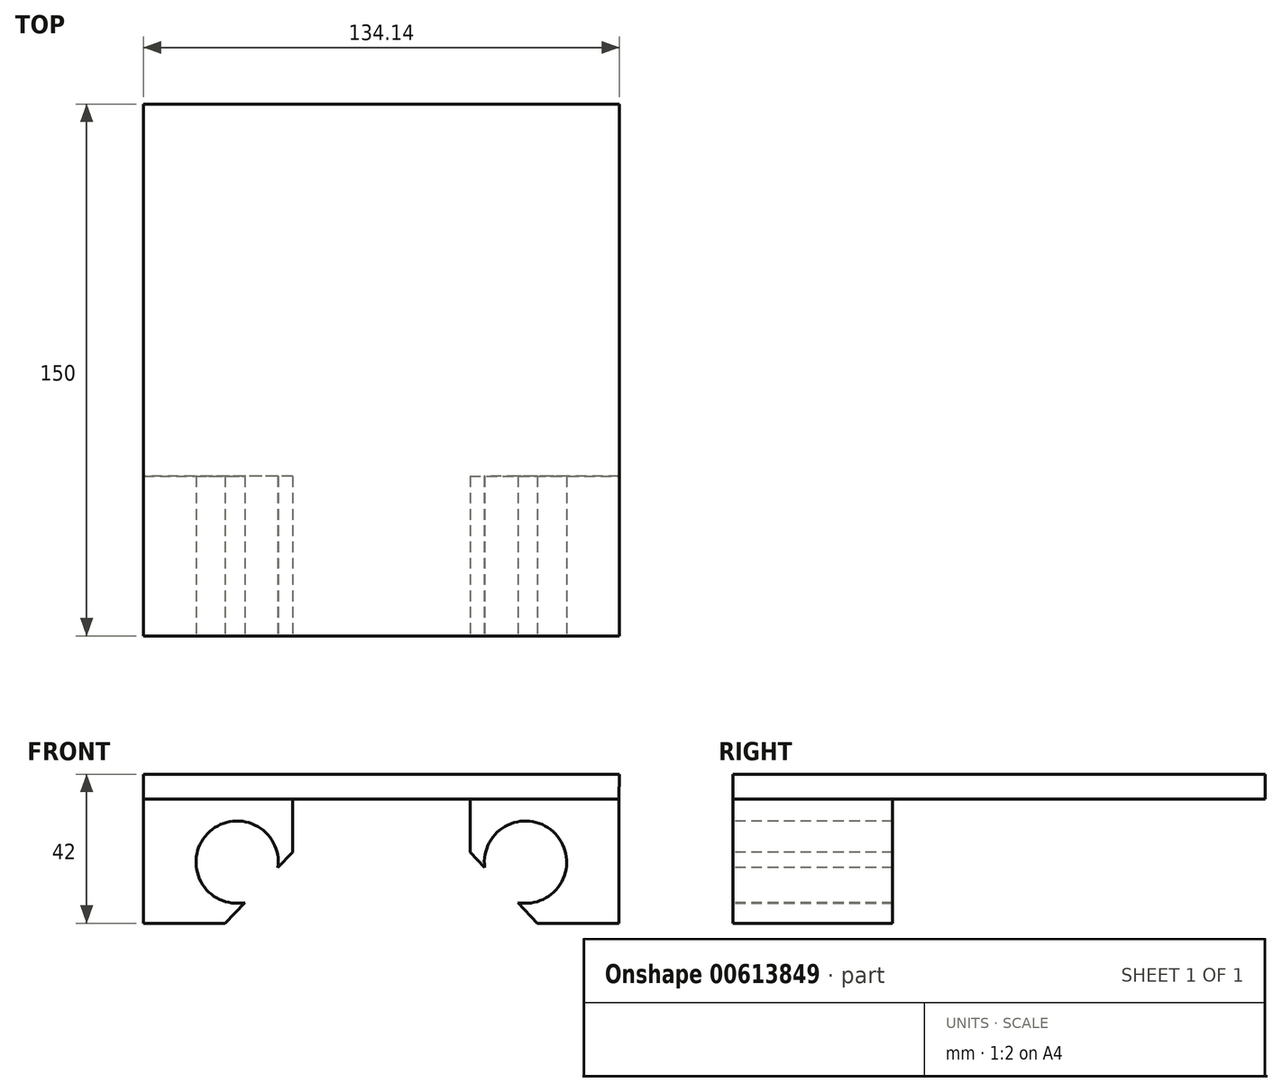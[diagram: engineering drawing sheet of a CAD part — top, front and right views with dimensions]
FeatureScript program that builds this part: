
annotation { "Feature Type Name" : "Feature", "Feature Type Description" : "" }
export const myFeature = defineFeature(function(context is Context, id is Id, definition is map)
    precondition{}
    {
        {
            var Q0;
            Q0=qCreatedBy(makeId("Front.planeOp"),FACE);
            var sketch = newSketch(context, id + "F0", { "sketchPlane" : qUnion([Q0])});
            skLineSegment(sketch, "E0", {"start": v(0, 35) * mm, "end": v(67, 35) * mm});
            skLineSegment(sketch, "E1", {"start": v(67, 35) * mm, "end": v(67, 0) * mm});
            skLineSegment(sketch, "E2", {"start": v(67, 0) * mm, "end": v(44, 0) * mm});
            skLineSegment(sketch, "E3", {"start": v(44, 0) * mm, "end": v(38.5, 5.8) * mm});
            skPoint(sketch, "E4", {"position": v(25, 35) * mm});
            skLineSegment(sketch, "E5", {"start": v(25, 35) * mm, "end": v(25, 20) * mm});
            skLineSegment(sketch, "E6", {"start": v(25, 20) * mm, "end": v(29.13, 15.65) * mm});
            skLineSegment(sketch, "E7", {"start": v(29.13, 15.65) * mm, "end": v(38.5, 5.8) * mm, "construction": true});
            skArc(sketch, "E8", {"start": v(38.5, 5.8) * mm, "mid": v(49.05, 25.2) * mm, "end": v(29.13, 15.65) * mm});
            skLineSegment(sketch, "E9", {"start": v(0, 35) * mm, "end": v(0, 42) * mm});
            skLineSegment(sketch, "E10", {"start": v(0, 42) * mm, "end": v(67.07, 42) * mm});
            skLineSegment(sketch, "E11", {"start": v(67.07, 42) * mm, "end": v(67, 35) * mm});
            skLineSegment(sketch, "E12.MirrorCS", {"start": v(0, 42) * mm, "end": v(-67.07, 42) * mm});
            skLineSegment(sketch, "E13.MirrorCS", {"start": v(0, 35) * mm, "end": v(-67, 35) * mm});
            skLineSegment(sketch, "E14.MirrorCS", {"start": v(-67.07, 42) * mm, "end": v(-67, 35) * mm});
            skLineSegment(sketch, "E15.MirrorCS", {"start": v(-67, 35) * mm, "end": v(-67, 0) * mm});
            skLineSegment(sketch, "E16.MirrorCS", {"start": v(-25, 35) * mm, "end": v(-25, 20) * mm});
            skLineSegment(sketch, "E17.MirrorCS", {"start": v(-25, 20) * mm, "end": v(-29.13, 15.65) * mm});
            skArc(sketch, "E18.MirrorCS", {"start": v(-38.5, 5.8) * mm, "mid": v(-49.05, 25.2) * mm, "end": v(-29.13, 15.65) * mm});
            skLineSegment(sketch, "E19.MirrorCS", {"start": v(-44, 0) * mm, "end": v(-38.5, 5.8) * mm});
            skLineSegment(sketch, "E20.MirrorCS", {"start": v(-67, 0) * mm, "end": v(-44, 0) * mm});
            skSolve(sketch);
        }
        {
            var Q0;
            {var subQ1=sQuery(id+"F0.wireOp",EDGE,"E15.MirrorCS");Q0=makeQuery(id+"F0.imprint","IMPRINT",FACE,{"disambiguationData":[TD([[makeQuery(id+"F0.imprint","IMPRINT",EDGE,{"derivedFrom":subQ1}),1.0]])]});}
            var Q1;
            {var subQ0=sQuery(id+"F0.wireOp",EDGE,"E1");Q1=makeQuery(id+"F0.imprint","IMPRINT",FACE,{"disambiguationData":[TD([[makeQuery(id+"F0.imprint","IMPRINT",EDGE,{"derivedFrom":subQ0}),-1.0]])]});}
            extrude(context, id + "F1", {"entities" : qUnion([Q0, Q1]), "oppositeDirection" : true, "depth" : 45 * mm, "offsetDistance" : 25 * mm});
        }
        {
            var Q0;
            {var subQ0=sQuery(id+"F0.wireOp",EDGE,"E9");Q0=makeQuery(id+"F0.imprint","IMPRINT",FACE,{"disambiguationData":[TD([[makeQuery(id+"F0.imprint","IMPRINT",EDGE,{"derivedFrom":subQ0}),-1.0]])]});}
            var Q1;
            {var subQ1=sQuery(id+"F0.wireOp",EDGE,"E9");Q1=makeQuery(id+"F0.imprint","IMPRINT",FACE,{"disambiguationData":[TD([[makeQuery(id+"F0.imprint","IMPRINT",EDGE,{"derivedFrom":subQ1}),1.0]])]});}
            extrude(context, id + "F2", {"entities" : qUnion([Q0, Q1]), "oppositeDirection" : true, "depth" : 150 * mm, "offsetDistance" : 25 * mm});
        }
        {
            var Q0;
            {var subQ1=sQuery(id+"F0.wireOp",EDGE,"E15.MirrorCS");Q0=makeQuery(id+"F0.imprint","IMPRINT",FACE,{"disambiguationData":[TD([[makeQuery(id+"F0.imprint","IMPRINT",EDGE,{"derivedFrom":subQ1}),1.0]])]});}
            var Q1;
            {var subQ0=sQuery(id+"F0.wireOp",EDGE,"E1");Q1=makeQuery(id+"F0.imprint","IMPRINT",FACE,{"disambiguationData":[TD([[makeQuery(id+"F0.imprint","IMPRINT",EDGE,{"derivedFrom":subQ0}),-1.0]])]});}
            extrude(context, id + "F3", {"entities" : qUnion([Q0, Q1]), "oppositeDirection" : true, "depth" : 45 * mm, "offsetDistance" : 25 * mm});
        }
    });
